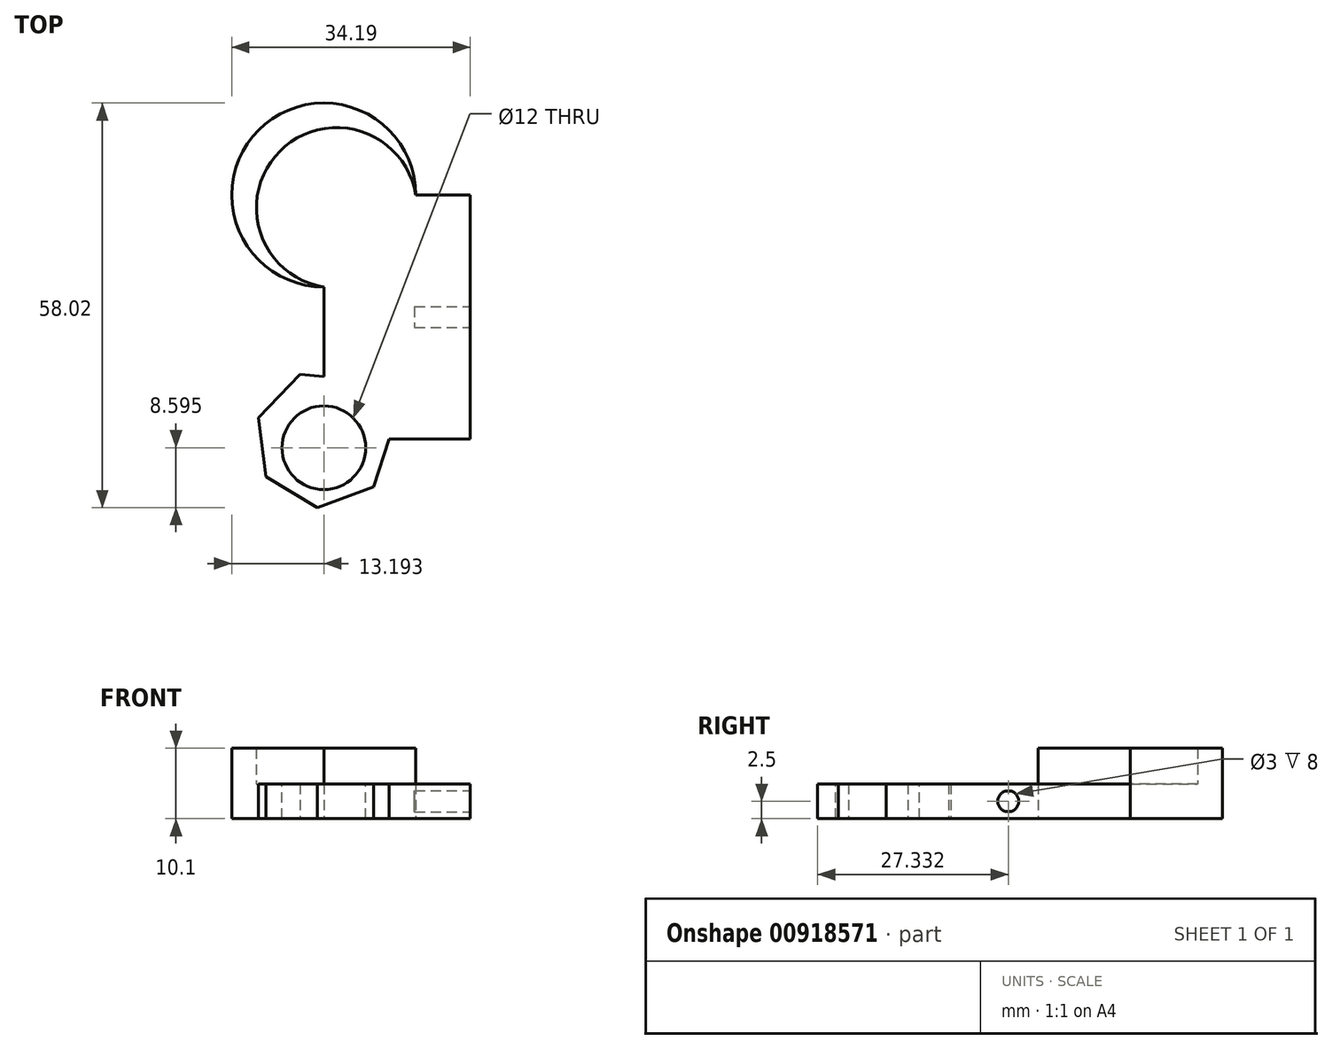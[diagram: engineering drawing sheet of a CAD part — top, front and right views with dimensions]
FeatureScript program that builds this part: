
annotation { "Feature Type Name" : "Feature", "Feature Type Description" : "" }
export const myFeature = defineFeature(function(context is Context, id is Id, definition is map)
    precondition{}
    {
        {
            var Q0;
            Q0=qCreatedBy(makeId("Top.planeOp"),FACE);
            var sketch = newSketch(context, id + "F0", { "sketchPlane" : qUnion([Q0])});
            skLineSegment(sketch, "E0.bottom", {"start": v(16.5, 12.77) * mm, "end": v(24.3, 12.77) * mm});
            skLineSegment(sketch, "E0.top", {"start": v(3.3, -22.23) * mm, "end": v(24.3, -22.23) * mm});
            skLineSegment(sketch, "E0.left", {"start": v(3.3, -0.42) * mm, "end": v(3.3, -22.23) * mm});
            skLineSegment(sketch, "E0.right", {"start": v(24.3, 12.77) * mm, "end": v(24.3, -22.23) * mm});
            skArc(sketch, "E1", {"start": v(16.5, 12.77) * mm, "mid": v(-6.03, 22.1) * mm, "end": v(3.3, -0.42) * mm});
            skArc(sketch, "E2.cCircle", {"start": v(4.14, -13.37) * mm, "mid": v(-3.28, -28.22) * mm, "end": v(12.2, -22.23) * mm, "construction": true});
            skLineSegment(sketch, "E2.0", {"start": v(10.41, -29.08) * mm, "end": v(2.38, -32.06) * mm});
            skLineSegment(sketch, "E2.1", {"start": v(2.38, -32.06) * mm, "end": v(-4.96, -27.64) * mm});
            skLineSegment(sketch, "E2.2", {"start": v(-4.96, -27.64) * mm, "end": v(-6.08, -19.14) * mm});
            skLineSegment(sketch, "E2.3", {"start": v(-6.08, -19.14) * mm, "end": v(-0.13, -12.97) * mm});
            skLineSegment(sketch, "E2.4", {"start": v(-0.13, -12.97) * mm, "end": v(4.14, -13.37) * mm});
            skLineSegment(sketch, "E2.6", {"start": v(12.67, -22.23) * mm, "end": v(10.41, -29.08) * mm});
            skPoint(sketch, "E2.0.midPoint", {"position": v(6.4, -30.57) * mm});
            skPoint(sketch, "E3.orphan", {"position": v(8.4, -13.77) * mm});
            skPoint(sketch, "E4.orphan", {"position": v(13.1, -20.94) * mm});
            skSolve(sketch);
        }
        {
            var Q0;
            Q0 = qSketchRegion(id + "F0", true);
            var Q1;
            Q1=makeQuery(id+"F0.imprint","IMPRINT",FACE,{"disambiguationData":[TD([[makeQuery(id+"F0.imprint","IMPRINT",EDGE,{"derivedFrom":sQuery(id+"F0.wireOp",EDGE,"E0.bottom")}),-1.0]])]});
            extrude(context, id + "F1", {"entities" : qUnion([Q0, Q1]), "depth" : 5 * mm, "offsetDistance" : 25 * mm});
        }
        {
            var Q0;
            Q0=makeQuery(id+"F1.opExtrude","CAP_FACE",FACE,{"disambiguationData":[OSD([sQuery(id+"F0.wireOp",EDGE,"E0.bottom"),sQuery(id+"F0.wireOp",EDGE,"E0.top"),sQuery(id+"F0.wireOp",EDGE,"E0.left"),sQuery(id+"F0.wireOp",EDGE,"E0.right"),sQuery(id+"F0.wireOp",EDGE,"E1"),sQuery(id+"F0.wireOp",EDGE,"E2.0"),sQuery(id+"F0.wireOp",EDGE,"E2.1"),sQuery(id+"F0.wireOp",EDGE,"E2.2"),sQuery(id+"F0.wireOp",EDGE,"E2.3"),sQuery(id+"F0.wireOp",EDGE,"E2.4"),sQuery(id+"F0.wireOp",EDGE,"E2.6")])],"isStart":false});
            var sketch = newSketch(context, id + "F2", { "sketchPlane" : qUnion([Q0])});
            skArc(sketch, "E5", {"start": v(16.5, 12.77) * mm, "mid": v(-2.99, 19.06) * mm, "end": v(3.3, -0.42) * mm});
            skSolve(sketch);
        }
        {
            var Q0;
            Q0=makeQuery(id+"F2.imprint","IMPRINT",FACE,{"disambiguationData":[TD([[makeQuery(id+"F2.imprint","IMPRINT",EDGE,{"derivedFrom":sQuery(id+"F2.wireOp",EDGE,"E5")}),-1.0]])]});
            extrude(context, id + "F3", {"entities" : qUnion([Q0]), "operationType" : NewBodyOperationType.ADD, "depth" : 5.1 * mm, "offsetDistance" : 25 * mm});
        }
        {
            var Q0;
            Q0=makeQuery(id+"F1.opExtrude","SWEPT_FACE",FACE,{"disambiguationData":[OSD([sQuery(id+"F0.wireOp",EDGE,"E0.right")])]});
            var sketch = newSketch(context, id + "F4", { "sketchPlane" : qUnion([Q0])});
            skCircle(sketch, "E6", {"center": v(-4.73, 2.5) * mm, "radius": 1.5 * mm});
            skPoint(sketch, "E6.centerSnap0", {"position": v(-22.23, 2.5) * mm});
            skPoint(sketch, "E6.centerSnap1", {"position": v(-4.73, 5) * mm});
            skSolve(sketch);
        }
        {
            var Q0;
            Q0=makeQuery(id+"F4.imprint","IMPRINT",FACE,{"disambiguationData":[TD([[makeQuery(id+"F4.imprint","IMPRINT",EDGE,{"derivedFrom":sQuery(id+"F4.wireOp",EDGE,"E6")}),1.0]])]});
            extrude(context, id + "F5", {"entities" : qUnion([Q0]), "operationType" : NewBodyOperationType.REMOVE, "oppositeDirection" : true, "depth" : 8 * mm, "offsetDistance" : 25 * mm});
        }
        {
            var Q0;
            Q0=makeQuery(id+"F1.opExtrude","CAP_FACE",FACE,{"disambiguationData":[OSD([sQuery(id+"F0.wireOp",EDGE,"E0.bottom"),sQuery(id+"F0.wireOp",EDGE,"E0.top"),sQuery(id+"F0.wireOp",EDGE,"E0.left"),sQuery(id+"F0.wireOp",EDGE,"E0.right"),sQuery(id+"F0.wireOp",EDGE,"E1"),sQuery(id+"F0.wireOp",EDGE,"E2.0"),sQuery(id+"F0.wireOp",EDGE,"E2.1"),sQuery(id+"F0.wireOp",EDGE,"E2.2"),sQuery(id+"F0.wireOp",EDGE,"E2.3"),sQuery(id+"F0.wireOp",EDGE,"E2.4"),sQuery(id+"F0.wireOp",EDGE,"E2.6")])],"isStart":false});
            var sketch = newSketch(context, id + "F6", { "sketchPlane" : qUnion([Q0])});
            skCircle(sketch, "E7", {"center": v(3.3, -23.47) * mm, "radius": 6 * mm});
            skSolve(sketch);
        }
        {
            var Q0;
            Q0 = qSketchRegion(id + "F6", true);
            var Q1;
            Q1=makeQuery(id+"F6.imprint","IMPRINT",FACE,{"disambiguationData":[TD([[makeQuery(id+"F6.imprint","IMPRINT",EDGE,{"derivedFrom":sQuery(id+"F6.wireOp",EDGE,"E7")}),1.0]])]});
            extrude(context, id + "F7", {"entities" : qUnion([Q0, Q1]), "operationType" : NewBodyOperationType.REMOVE, "oppositeDirection" : true, "depth" : 25 * mm, "offsetDistance" : 25 * mm});
        }
    });
